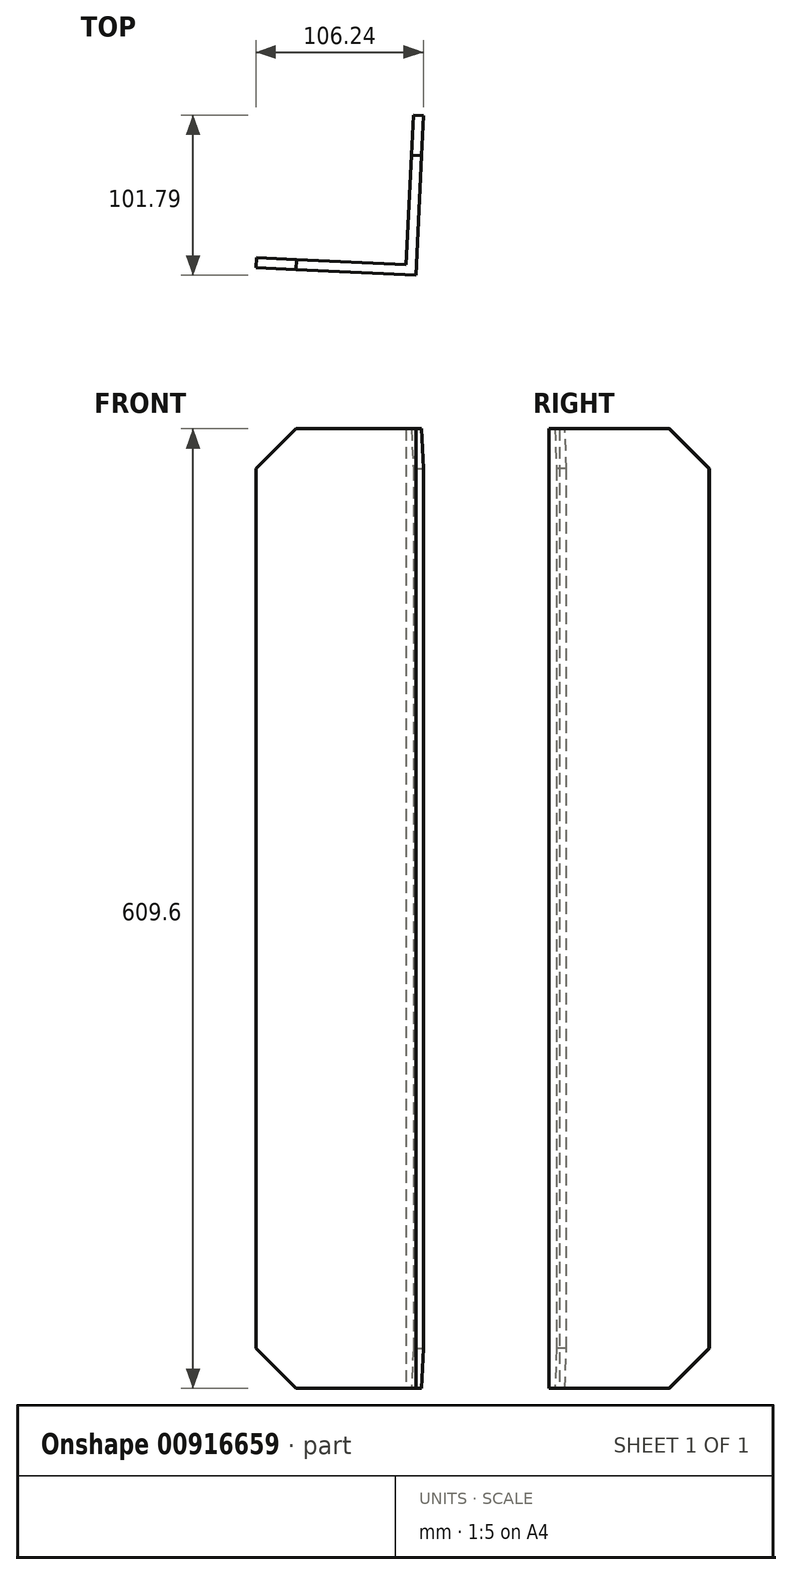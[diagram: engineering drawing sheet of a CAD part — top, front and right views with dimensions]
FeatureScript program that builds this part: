
annotation { "Feature Type Name" : "Feature", "Feature Type Description" : "" }
export const myFeature = defineFeature(function(context is Context, id is Id, definition is map)
    precondition{}
    {
        {
            var Q0;
            Q0=qCreatedBy(makeId("Top.planeOp"),FACE);
            var sketch = newSketch(context, id + "F0", { "sketchPlane" : qUnion([Q0])});
            skLineSegment(sketch, "E0", {"start": v(21.2, -33.84) * mm, "end": v(122.7, -38.6) * mm});
            skLineSegment(sketch, "E1", {"start": v(122.7, -38.6) * mm, "end": v(127.45, 62.89) * mm});
            skLineSegment(sketch, "E2", {"start": v(21.2, -33.84) * mm, "end": v(21.2, -27.5) * mm});
            skLineSegment(sketch, "E3", {"start": v(127.45, 62.89) * mm, "end": v(121.1, 63.19) * mm});
            skLineSegment(sketch, "E4", {"start": v(21.2, -27.5) * mm, "end": v(116.55, -31.96) * mm});
            skLineSegment(sketch, "E5", {"start": v(116.55, -31.96) * mm, "end": v(121.1, 63.19) * mm});
            skSolve(sketch);
        }
        {
            var Q0;
            Q0 = qSketchRegion(id + "F0", true);
            extrude(context, id + "F1", {"entities" : qUnion([Q0]), "depth" : 609.6 * mm, "offsetDistance" : 25.4 * mm});
        }
        {
            var Q0;
            Q0=makeQuery(id+"F1.opExtrude","SWEPT_FACE",FACE,{"disambiguationData":[OSD([sQuery(id+"F0.wireOp",EDGE,"E1")])]});
            var sketch = newSketch(context, id + "F2", { "sketchPlane" : qUnion([Q0])});
            skLineSegment(sketch, "E6", {"start": v(68.79, 584.2) * mm, "end": v(43.39, 609.6) * mm});
            skSolve(sketch);
        }
        {
            var Q0;
            Q0 = qSketchRegion(id + "F2", true);
            var Q1;
            {var subQ0=sQuery(id+"F2.wireOp",EDGE,"E6");Q1=makeQuery(id+"F2.imprint","IMPRINT",FACE,{"disambiguationData":[TD([[makeQuery(id+"F2.imprint","IMPRINT",EDGE,{"derivedFrom":subQ0}),-1.0]])]});}
            extrude(context, id + "F3", {"entities" : qUnion([Q0, Q1]), "operationType" : NewBodyOperationType.REMOVE, "oppositeDirection" : true, "depth" : 25.4 * mm, "offsetDistance" : 25.4 * mm});
        }
        {
            var Q0;
            Q0=makeQuery(id+"F1.opExtrude","SWEPT_FACE",FACE,{"disambiguationData":[OSD([sQuery(id+"F0.wireOp",EDGE,"E0")])]});
            var sketch = newSketch(context, id + "F4", { "sketchPlane" : qUnion([Q0])});
            skLineSegment(sketch, "E7", {"start": v(48.17, 609.6) * mm, "end": v(22.77, 584.2) * mm});
            skSolve(sketch);
        }
        {
            var Q0;
            Q0 = qSketchRegion(id + "F4", true);
            var Q1;
            {var subQ0=sQuery(id+"F4.wireOp",EDGE,"E7");Q1=makeQuery(id+"F4.imprint","IMPRINT",FACE,{"disambiguationData":[TD([[makeQuery(id+"F4.imprint","IMPRINT",EDGE,{"derivedFrom":subQ0}),-1.0]])]});}
            var Q2;
            Q2=makeQuery(id+"F1.opExtrude","SWEPT_FACE",FACE,{"disambiguationData":[OSD([sQuery(id+"F0.wireOp",EDGE,"E2")])]});
            extrude(context, id + "F5", {"entities" : qUnion([Q0, Q1, Q2]), "operationType" : NewBodyOperationType.REMOVE, "oppositeDirection" : true, "depth" : 25.4 * mm, "offsetDistance" : 25.4 * mm});
        }
        {
            var Q0;
            Q0=makeQuery(id+"F1.opExtrude","SWEPT_FACE",FACE,{"disambiguationData":[OSD([sQuery(id+"F0.wireOp",EDGE,"E0")])]});
            var sketch = newSketch(context, id + "F6", { "sketchPlane" : qUnion([Q0])});
            skLineSegment(sketch, "E8", {"start": v(22.77, 25.4) * mm, "end": v(48.17, 0) * mm});
            skSolve(sketch);
        }
        {
            var Q0;
            Q0 = qSketchRegion(id + "F6", true);
            var Q1;
            {var subQ0=sQuery(id+"F6.wireOp",EDGE,"E8");Q1=makeQuery(id+"F6.imprint","IMPRINT",FACE,{"disambiguationData":[TD([[makeQuery(id+"F6.imprint","IMPRINT",EDGE,{"derivedFrom":subQ0}),-1.0]])]});}
            extrude(context, id + "F7", {"entities" : qUnion([Q0, Q1]), "operationType" : NewBodyOperationType.REMOVE, "oppositeDirection" : true, "depth" : 25.4 * mm, "offsetDistance" : 25.4 * mm});
        }
        {
            var Q0;
            Q0=makeQuery(id+"F1.opExtrude","SWEPT_FACE",FACE,{"disambiguationData":[OSD([sQuery(id+"F0.wireOp",EDGE,"E1")])]});
            var sketch = newSketch(context, id + "F8", { "sketchPlane" : qUnion([Q0])});
            skLineSegment(sketch, "E9", {"start": v(43.39, 0) * mm, "end": v(68.79, 25.4) * mm});
            skSolve(sketch);
        }
        {
            var Q0;
            Q0 = qSketchRegion(id + "F8", true);
            var Q1;
            {var subQ0=sQuery(id+"F8.wireOp",EDGE,"E9");Q1=makeQuery(id+"F8.imprint","IMPRINT",FACE,{"disambiguationData":[TD([[makeQuery(id+"F8.imprint","IMPRINT",EDGE,{"derivedFrom":subQ0}),-1.0]])]});}
            extrude(context, id + "F9", {"entities" : qUnion([Q0, Q1]), "operationType" : NewBodyOperationType.REMOVE, "oppositeDirection" : true, "depth" : 25.4 * mm, "offsetDistance" : 25.4 * mm});
        }
    });
